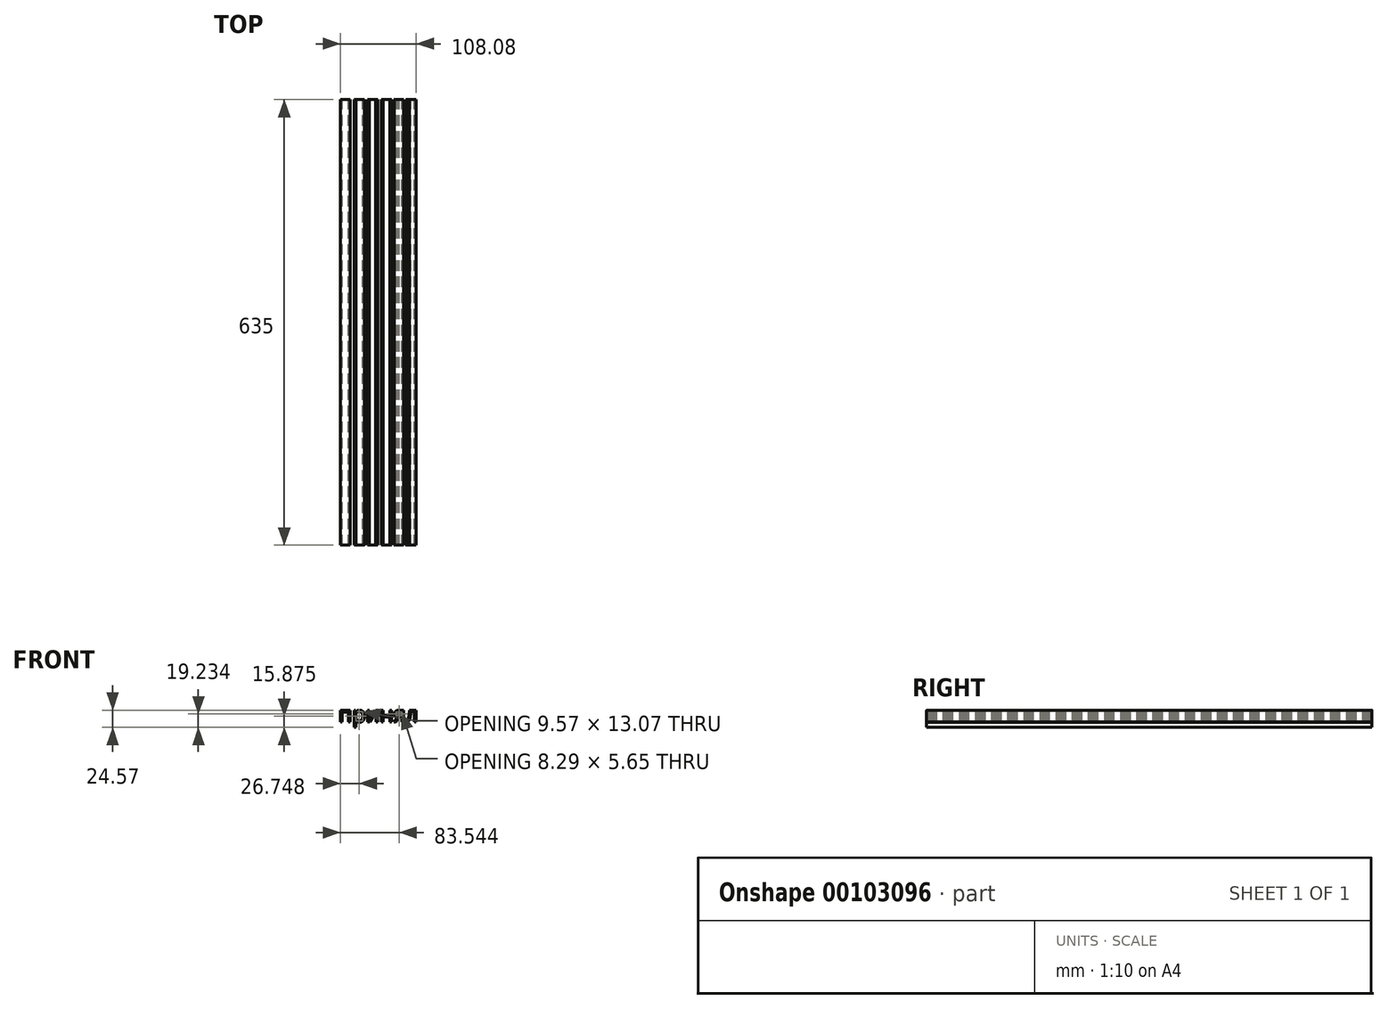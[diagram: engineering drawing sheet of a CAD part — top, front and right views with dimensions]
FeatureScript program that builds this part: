
annotation { "Feature Type Name" : "Feature", "Feature Type Description" : "" }
export const myFeature = defineFeature(function(context is Context, id is Id, definition is map)
    precondition{}
    {
        {
            var Q0;
            Q0=qCreatedBy(makeId("Front.planeOp"),FACE);
            var sketch = newSketch(context, id + "F2", { "sketchPlane" : qUnion([Q0])});
            skLineSegment(sketch, "E0.bottom", {"start": v(-30.7, 17.81) * mm, "end": v(87.11, 17.81) * mm});
            skLineSegment(sketch, "E0.top", {"start": v(-30.7, 29.23) * mm, "end": v(87.11, 29.23) * mm});
            skLineSegment(sketch, "E0.left", {"start": v(-30.7, 17.81) * mm, "end": v(-30.7, 29.23) * mm});
            skLineSegment(sketch, "E0.right", {"start": v(87.11, 17.81) * mm, "end": v(87.11, 29.23) * mm});
            skLineSegment(sketch, "E1.bottom", {"start": v(57.66, 71.77) * mm, "end": v(40.34, 71.77) * mm});
            skLineSegment(sketch, "E1.top", {"start": v(57.66, 29.23) * mm, "end": v(40.34, 29.23) * mm});
            skLineSegment(sketch, "E1.left", {"start": v(57.66, 71.77) * mm, "end": v(57.66, 29.23) * mm});
            skLineSegment(sketch, "E1.right", {"start": v(40.34, 71.77) * mm, "end": v(40.34, 29.23) * mm});
            skSolve(sketch);
        }
        {
            var Q0;
            Q0 = qSketchRegion(id + "F2", true);
            var sketch = newSketch(context, id + "F0", { "sketchPlane" : qUnion([Q0])});
            skText(sketch, "E2", { "text": "принял", "fontName": "OpenSans-Regular.ttf"});
            const initialGuessF0  = {"E2": [-0.0472, 0.03305, 1, 0, 0.02252]};
            skSetInitialGuess(sketch, initialGuessF0);
            skSolve(sketch);
        }
        {
            var Q0;
            Q0 = qSketchRegion(id + "F0", true);
            extrude(context, id + "F1", {"entities" : qUnion([Q0]), "depth" : 635 * mm});
        }
    });
